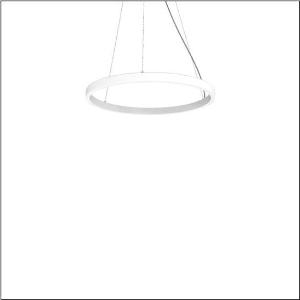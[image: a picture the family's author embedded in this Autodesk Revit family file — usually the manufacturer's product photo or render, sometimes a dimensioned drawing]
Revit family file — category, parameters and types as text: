
# Revit family: silica_r__21_ring-o_5pjbo2d1004a_430d
name_source: partatom
category: Lighting Fixtures
units: mm (PartAtom-declared; Revit-internal decimal feet)

## family parameters
Cut with Voids When Loaded = No
Host = Face
Light Source = No
Part Type = Normal
Room Calculation Point = No
Round Connector Dimension = Use Diameter
Shared = No

## types (1)
- Silica® 21 Ring-O (1 x LED, 4700 lm, 80 W, 3000K)
    Apparent Load = 80 VA
    CIE Flux Codes = 2 16 49 50 100
    Color Rendering = 80
    Color Temperature = 3000K
    Default Elevation = 1800 mm
    Description = Silica® 21 Ring-O, suspended luminaire, of PMMA, frosted, light emission: outer ring side luminous distribution, primary light characteristic: symmetric, installation type: suspended mounting, LED, rated luminous flux: 4.700lm, luminous efficacy: 59lm/W, light colour: 830, colour temperature: 3000K, with terminal, 5-pole, mains connection: 230V, AC/DC, 0/50..60Hz, rated input power: 80W, housing, of extruded aluminium section, traffic white (RAL 9016), diameter: 810mm, ceiling canopy, traffic white (RAL 9016), protection rating (lamp compartment): IP40, insulation class (complete): insulation class I (protective earthing), certification: CE, impact resistance: IK02, permissible operating ambient temperature: 0..+35°C, packaging unit: 1 piece
    Height = 48 mm  [stored 0.15748 ft]
    Lamp = 1 x LED
    Lamp Light Flux = 4700 lm
    Lamp Power = 80 W
    Lamp count = 1
    Length = 810 mm
    Luminous efficacy = 59 lm/W
    Manufacturer = Siteco
    ModVariant = No
    Model = 5PJBO2D1004A
    Mounting Place = Ceiling
    Mounting Type = Pendant
    Number of Poles = 1
    OnlyDefault = Yes
    Power Factor = 1
    Product Name = Silica® 21 Ring-O
    Product group = suspended luminaire
    ProductGroupID = 904
    Protection Class = Protection class I
    Protection Degree = IP 40
    RLX_Detail_Level = 1
    RLX_Emergency_Light_Flux = 0 lm
    RLX_Emergency_Type = 0
    RLX_Emergency_Type_DB = No
    RlxData = <blob elided: 11977 chars, md5=511c05bb>
    Socket = socket
    Standby Power = 0 W
    System Light Flux = 4700 lm
    System Power = 80 W
    Type Comments = Product without accessories
    Type Image = l_1258383.jpg
    URL = http://relux.com
    VarID = ---
    Voltage = 0 V
    Weight = 0.00 kg
    Width = 0 mm  [stored 0 ft]

note: [stored X ft] marks values corroborated as IEEE doubles in the binary element streams (Revit-internal decimal feet)

## geometry (parser evidence)
native form markers: Sweep x14
no freeform markers — native parametric forms only
